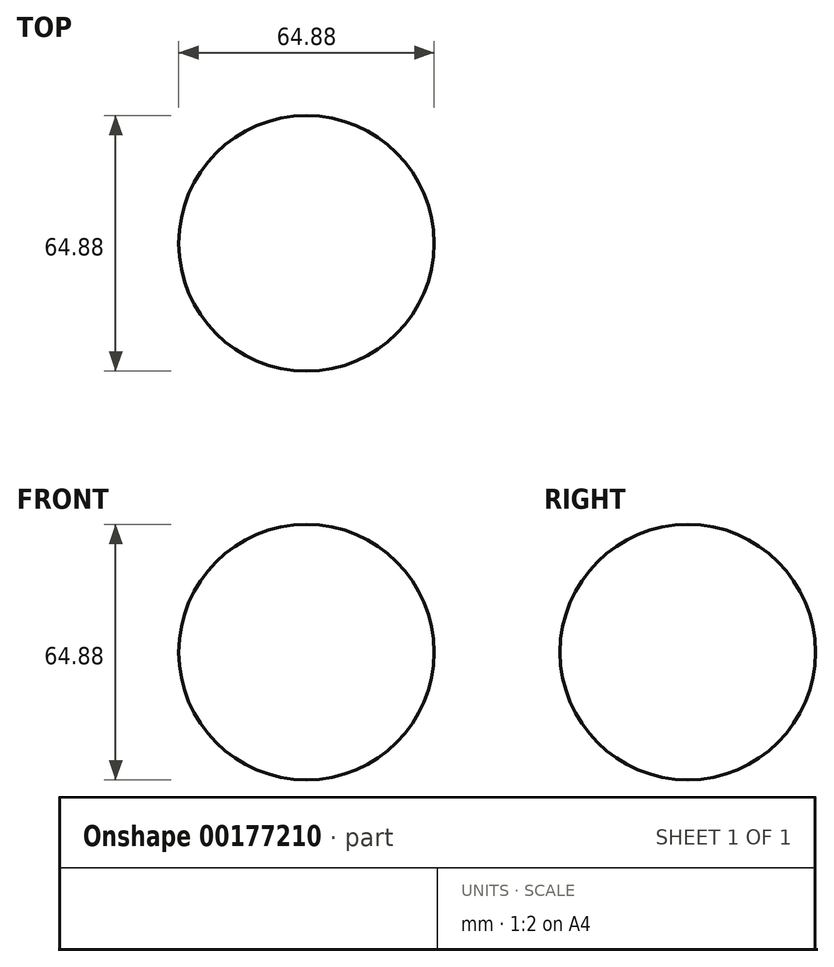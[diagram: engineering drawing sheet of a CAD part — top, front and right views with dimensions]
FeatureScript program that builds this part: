
annotation { "Feature Type Name" : "Feature", "Feature Type Description" : "" }
export const myFeature = defineFeature(function(context is Context, id is Id, definition is map)
    precondition{}
    {
        {
            var Q0;
            Q0=qCreatedBy(makeId("Top.planeOp"),FACE);
            var sketch = newSketch(context, id + "F0", { "sketchPlane" : qUnion([Q0])});
            skArc(sketch, "E0", {"start": v(0, -32.44) * mm, "mid": v(32.44, 0) * mm, "end": v(0, 32.44) * mm});
            skLineSegment(sketch, "E1", {"start": v(0, 0) * mm, "end": v(0, 32.44) * mm});
            skLineSegment(sketch, "E2", {"start": v(0, 0) * mm, "end": v(0, -32.44) * mm});
            skSolve(sketch);
        }
        {
            var Q0;
            Q0 = qSketchRegion(id + "F0", true);
            var Q1;
            Q1=sQuery(id+"F0.wireOp",EDGE,"E2");
            revolve(context, id + "F1", {"entities" : qUnion([Q0]), "axis" : qUnion([Q1]), "revolveType" : RevolveType.FULL});
        }
    });
